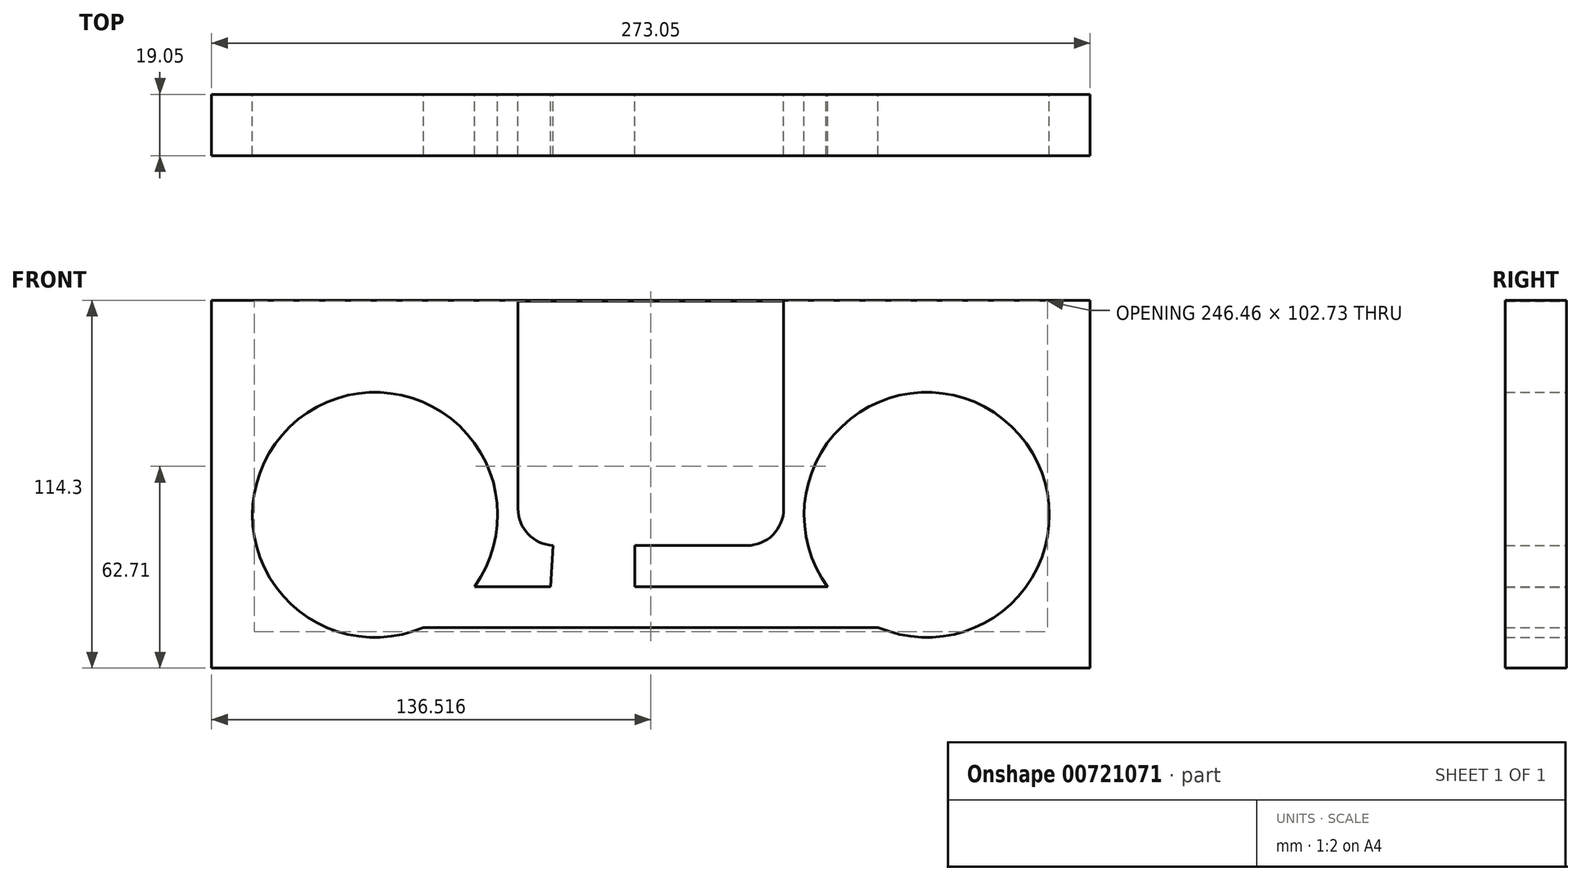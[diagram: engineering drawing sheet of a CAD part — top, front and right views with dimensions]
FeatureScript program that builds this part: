
annotation { "Feature Type Name" : "Feature", "Feature Type Description" : "" }
export const myFeature = defineFeature(function(context is Context, id is Id, definition is map)
    precondition{}
    {
        {
            var Q0;
            Q0=qCreatedBy(makeId("Front.planeOp"),FACE);
            var sketch = newSketch(context, id + "F0", { "sketchPlane" : qUnion([Q0])});
            skLineSegment(sketch, "E0.bottom", {"start": v(0, 0) * mm, "end": v(273.05, 0) * mm});
            skLineSegment(sketch, "E0.top", {"start": v(0, 114.3) * mm, "end": v(273.05, 114.3) * mm});
            skLineSegment(sketch, "E0.left", {"start": v(0, 0) * mm, "end": v(0, 114.3) * mm});
            skLineSegment(sketch, "E0.right", {"start": v(273.05, 0) * mm, "end": v(273.05, 114.3) * mm});
            skSolve(sketch);
        }
        {
            var Q0;
            Q0=qSketchRegion(id+"F0",true);
            extrude(context, id + "F1", {"entities" : qUnion([Q0]), "depth" : 19.05 * mm, "offsetDistance" : 25.4 * mm});
        }
        {
            var Q0;
            Q0=qCreatedBy(makeId("Front.planeOp"),FACE);
            var sketch = newSketch(context, id + "F2", { "sketchPlane" : qUnion([Q0])});
            skCircle(sketch, "E1", {"center": v(50.8, 47.63) * mm, "radius": 38.1 * mm});
            skCircle(sketch, "E2", {"center": v(222.25, 47.63) * mm, "radius": 38.1 * mm});
            skSolve(sketch);
        }
        {
            var Q0;
            Q0=makeQuery(id+"F2.imprint","IMPRINT",FACE,{"disambiguationData":[TD([[makeQuery(id+"F2.imprint","IMPRINT",EDGE,{"derivedFrom":sQuery(id+"F2.wireOp",EDGE,"E1")}),1.0]])]});
            var Q1;
            Q1=makeQuery(id+"F2.imprint","IMPRINT",FACE,{"disambiguationData":[TD([[makeQuery(id+"F2.imprint","IMPRINT",EDGE,{"derivedFrom":sQuery(id+"F2.wireOp",EDGE,"E2")}),1.0]])]});
            extrude(context, id + "F3", {"entities" : qUnion([Q0, Q1]), "operationType" : NewBodyOperationType.REMOVE, "depth" : 25.4 * mm, "offsetDistance" : 25.4 * mm});
        }
        {
            var Q0;
            Q0=qCreatedBy(makeId("Front.planeOp"),FACE);
            var sketch = newSketch(context, id + "F4", { "sketchPlane" : qUnion([Q0])});
            skLineSegment(sketch, "E3", {"start": v(95.25, 114.07) * mm, "end": v(95.25, 49.53) * mm});
            skLineSegment(sketch, "E4", {"start": v(106.68, 38.1) * mm, "end": v(166.37, 38.1) * mm});
            skLineSegment(sketch, "E5", {"start": v(177.8, 49.53) * mm, "end": v(177.8, 114.07) * mm});
            skPoint(sketch, "E6.visualSharp", {"position": v(95.25, 38.1) * mm});
            skArc(sketch, "E6.filletArc", {"start": v(95.25, 49.53) * mm, "mid": v(98.6, 41.45) * mm, "end": v(106.68, 38.1) * mm});
            skPoint(sketch, "E7.visualSharp", {"position": v(177.8, 38.1) * mm});
            skArc(sketch, "E7.filletArc", {"start": v(166.37, 38.1) * mm, "mid": v(174.45, 41.45) * mm, "end": v(177.8, 49.53) * mm});
            skLineSegment(sketch, "E8", {"start": v(95.25, 114.07) * mm, "end": v(177.8, 114.07) * mm});
            skSolve(sketch);
        }
        {
            var Q0;
            Q0 = qSketchRegion(id + "F4", true);
            extrude(context, id + "F5", {"entities" : qUnion([Q0]), "operationType" : NewBodyOperationType.REMOVE, "oppositeDirection" : true, "depth" : 25.4 * mm, "offsetDistance" : 25.4 * mm});
        }
        {
            var Q0;
            Q0 = qSketchRegion(id + "F4", true);
            extrude(context, id + "F6", {"entities" : qUnion([Q0]), "operationType" : NewBodyOperationType.REMOVE, "depth" : 25.4 * mm, "offsetDistance" : 25.4 * mm});
        }
        {
            var Q0;
            Q0=qCreatedBy(makeId("Front.planeOp"),FACE);
            var sketch = newSketch(context, id + "F7", { "sketchPlane" : qUnion([Q0])});
            skLineSegment(sketch, "E9", {"start": v(106.07, 38.33) * mm, "end": v(131.47, 38.33) * mm});
            skLineSegment(sketch, "E10", {"start": v(131.47, 38.33) * mm, "end": v(131.47, 25.35) * mm});
            skLineSegment(sketch, "E11", {"start": v(131.47, 25.35) * mm, "end": v(191, 25.35) * mm});
            skLineSegment(sketch, "E12", {"start": v(191, 25.35) * mm, "end": v(220.39, 12.65) * mm});
            skLineSegment(sketch, "E13", {"start": v(220.39, 12.65) * mm, "end": v(50.9, 12.65) * mm});
            skLineSegment(sketch, "E14", {"start": v(50.9, 12.65) * mm, "end": v(79.91, 25.35) * mm});
            skLineSegment(sketch, "E15", {"start": v(79.91, 25.35) * mm, "end": v(105.31, 25.35) * mm});
            skLineSegment(sketch, "E16", {"start": v(105.31, 25.35) * mm, "end": v(106.07, 38.33) * mm});
            skSolve(sketch);
        }
        {
            var Q0;
            Q0 = qSketchRegion(id + "F7", true);
            extrude(context, id + "F8", {"entities" : qUnion([Q0]), "operationType" : NewBodyOperationType.REMOVE, "depth" : 25.4 * mm, "offsetDistance" : 25.4 * mm});
        }
    });
